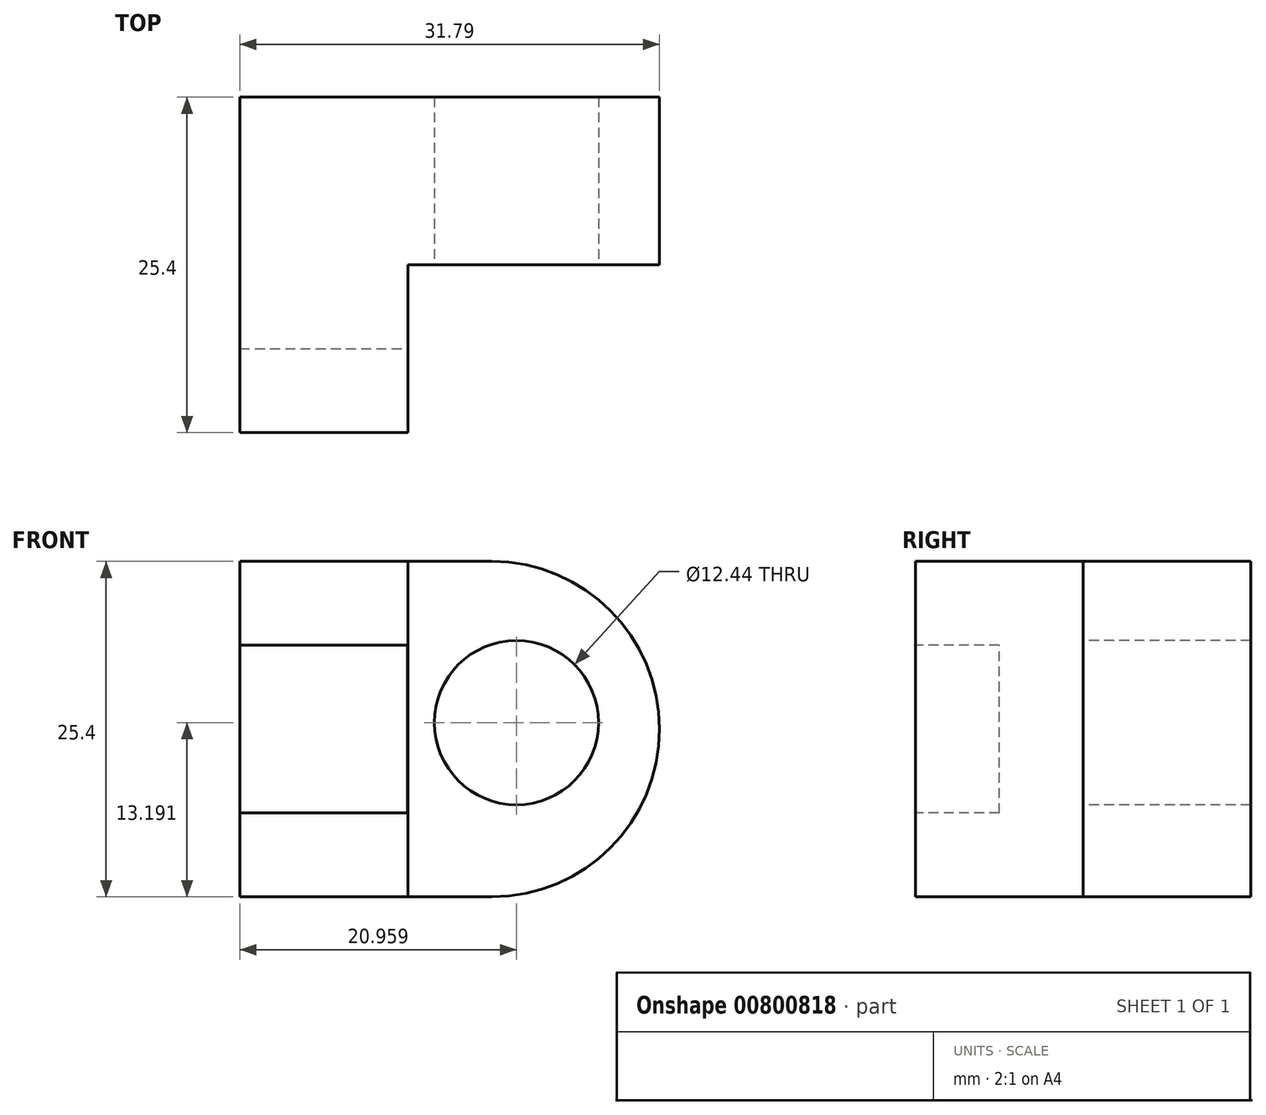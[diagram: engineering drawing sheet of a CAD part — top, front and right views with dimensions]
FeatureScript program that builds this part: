
annotation { "Feature Type Name" : "Feature", "Feature Type Description" : "" }
export const myFeature = defineFeature(function(context is Context, id is Id, definition is map)
    precondition{}
    {
        {
            var Q0;
            Q0=qCreatedBy(makeId("Front.planeOp"),FACE);
            var sketch = newSketch(context, id + "F0", { "sketchPlane" : qUnion([Q0])});
            skLineSegment(sketch, "E0", {"start": v(0, 0) * mm, "end": v(44.45, 0) * mm});
            skLineSegment(sketch, "E1", {"start": v(0, 0) * mm, "end": v(0, 25.4) * mm});
            skLineSegment(sketch, "E2", {"start": v(0, 25.4) * mm, "end": v(44.45, 25.4) * mm});
            skLineSegment(sketch, "E3", {"start": v(44.45, 25.4) * mm, "end": v(44.45, 0) * mm});
            skSolve(sketch);
        }
        {
            var Q0;
            Q0=makeQuery(id+"F0.imprint","IMPRINT",FACE,{"disambiguationData":[TD([[makeQuery(id+"F0.imprint","IMPRINT",EDGE,{"derivedFrom":sQuery(id+"F0.wireOp",EDGE,"E0")}),1.0]])]});
            extrude(context, id + "F1", {"entities" : qUnion([Q0]), "depth" : 25.4 * mm, "offsetDistance" : 25.4 * mm});
        }
        {
            var Q0;
            Q0=makeQuery(id+"F1.opExtrude","CAP_FACE",FACE,{"disambiguationData":[OSD([sQuery(id+"F0.wireOp",EDGE,"E0"),sQuery(id+"F0.wireOp",EDGE,"E1"),sQuery(id+"F0.wireOp",EDGE,"E2"),sQuery(id+"F0.wireOp",EDGE,"E3")])],"isStart":false});
            var sketch = newSketch(context, id + "F2", { "sketchPlane" : qUnion([Q0])});
            skLineSegment(sketch, "E4", {"start": v(0, 0) * mm, "end": v(0, 6.35) * mm});
            skLineSegment(sketch, "E5", {"start": v(0, 6.35) * mm, "end": v(12.7, 6.35) * mm});
            skLineSegment(sketch, "E6", {"start": v(12.7, 6.35) * mm, "end": v(12.7, 0) * mm});
            skLineSegment(sketch, "E7", {"start": v(12.7, 6.35) * mm, "end": v(12.7, 25.4) * mm});
            skLineSegment(sketch, "E8", {"start": v(0, 25.4) * mm, "end": v(0, 19.05) * mm});
            skLineSegment(sketch, "E9", {"start": v(0, 19.05) * mm, "end": v(12.7, 19.05) * mm});
            skSolve(sketch);
        }
        {
            var Q0;
            {var subQ0=sQuery(id+"F2.wireOp",EDGE,"E5");Q0=makeQuery(id+"F2.imprint","IMPRINT",FACE,{"disambiguationData":[TD([[makeQuery(id+"F2.imprint","IMPRINT",EDGE,{"derivedFrom":subQ0}),1.0]])]});}
            extrude(context, id + "F3", {"entities" : qUnion([Q0]), "operationType" : NewBodyOperationType.REMOVE, "oppositeDirection" : true, "depth" : 6.35 * mm, "offsetDistance" : 25.4 * mm});
        }
        {
            var Q0;
            Q0=makeQuery(id+"F1.opExtrude","CAP_FACE",FACE,{"disambiguationData":[OSD([sQuery(id+"F0.wireOp",EDGE,"E0"),sQuery(id+"F0.wireOp",EDGE,"E1"),sQuery(id+"F0.wireOp",EDGE,"E2"),sQuery(id+"F0.wireOp",EDGE,"E3")])],"isStart":false});
            var sketch = newSketch(context, id + "F4", { "sketchPlane" : qUnion([Q0])});
            skLineSegment(sketch, "E10", {"start": v(12.74, 25.4) * mm, "end": v(12.74, 0) * mm});
            skSolve(sketch);
        }
        {
            var Q0;
            {var subQ0=sQuery(id+"F4.wireOp",EDGE,"E10");Q0=makeQuery(id+"F4.imprint","IMPRINT",FACE,{"disambiguationData":[TD([[makeQuery(id+"F4.imprint","IMPRINT",EDGE,{"derivedFrom":subQ0}),1.0]])]});}
            extrude(context, id + "F5", {"entities" : qUnion([Q0]), "operationType" : NewBodyOperationType.REMOVE, "oppositeDirection" : true, "depth" : 12.7 * mm, "offsetDistance" : 25.4 * mm});
        }
        {
            var Q0;
            Q0=makeQuery(id+"F5.boolean.opBoolean","COPY",FACE,{"derivedFrom":makeQuery(id+"F5.opExtrude","CAP_FACE",FACE,{"disambiguationData":[OSD([sQuery(id+"F0.wireOp",EDGE,"E0"),sQuery(id+"F0.wireOp",EDGE,"E2"),sQuery(id+"F0.wireOp",EDGE,"E3"),sQuery(id+"F4.wireOp",EDGE,"E10")])],"isStart":false})});
            var sketch = newSketch(context, id + "F6", { "sketchPlane" : qUnion([Q0])});
            skLineSegment(sketch, "E11", {"start": v(12.74, 25.4) * mm, "end": v(19.1, 25.4) * mm});
            skArc(sketch, "E12", {"start": v(19.1, 0) * mm, "mid": v(31.8, 12.7) * mm, "end": v(19.1, 25.4) * mm});
            skSolve(sketch);
        }
        {
            var Q0;
            {var subQ0=sQuery(id+"F6.wireOp",EDGE,"E12");Q0=makeQuery(id+"F6.imprint","IMPRINT",FACE,{"disambiguationData":[TD([[makeQuery(id+"F6.imprint","IMPRINT",EDGE,{"derivedFrom":subQ0}),-1.0]])]});}
            extrude(context, id + "F7", {"entities" : qUnion([Q0]), "operationType" : NewBodyOperationType.REMOVE, "oppositeDirection" : true, "depth" : 25.4 * mm, "offsetDistance" : 25.4 * mm});
        }
        {
            var Q0;
            Q0=makeQuery(id+"F5.boolean.opBoolean","COPY",FACE,{"derivedFrom":makeQuery(id+"F5.opExtrude","CAP_FACE",FACE,{"disambiguationData":[OSD([sQuery(id+"F0.wireOp",EDGE,"E0"),sQuery(id+"F0.wireOp",EDGE,"E2"),sQuery(id+"F0.wireOp",EDGE,"E3"),sQuery(id+"F4.wireOp",EDGE,"E10")])],"isStart":false})});
            var sketch = newSketch(context, id + "F8", { "sketchPlane" : qUnion([Q0])});
            skLineSegment(sketch, "E13", {"start": v(19.1, 25.4) * mm, "end": v(19.1, 0) * mm, "construction": true});
            skLineSegment(sketch, "E14", {"start": v(12.74, 13.2) * mm, "end": v(31.78, 13.2) * mm, "construction": true});
            skCircle(sketch, "E15", {"center": v(20.96, 13.2) * mm, "radius": 6.22 * mm});
            skSolve(sketch);
        }
        {
            var Q0;
            Q0=makeQuery(id+"F8.imprint","IMPRINT",FACE,{"disambiguationData":[TD([[makeQuery(id+"F8.imprint","IMPRINT",EDGE,{"derivedFrom":sQuery(id+"F8.wireOp",EDGE,"E15")}),1.0]])]});
            extrude(context, id + "F9", {"entities" : qUnion([Q0]), "operationType" : NewBodyOperationType.REMOVE, "oppositeDirection" : true, "depth" : 25.4 * mm, "offsetDistance" : 25.4 * mm});
        }
    });
